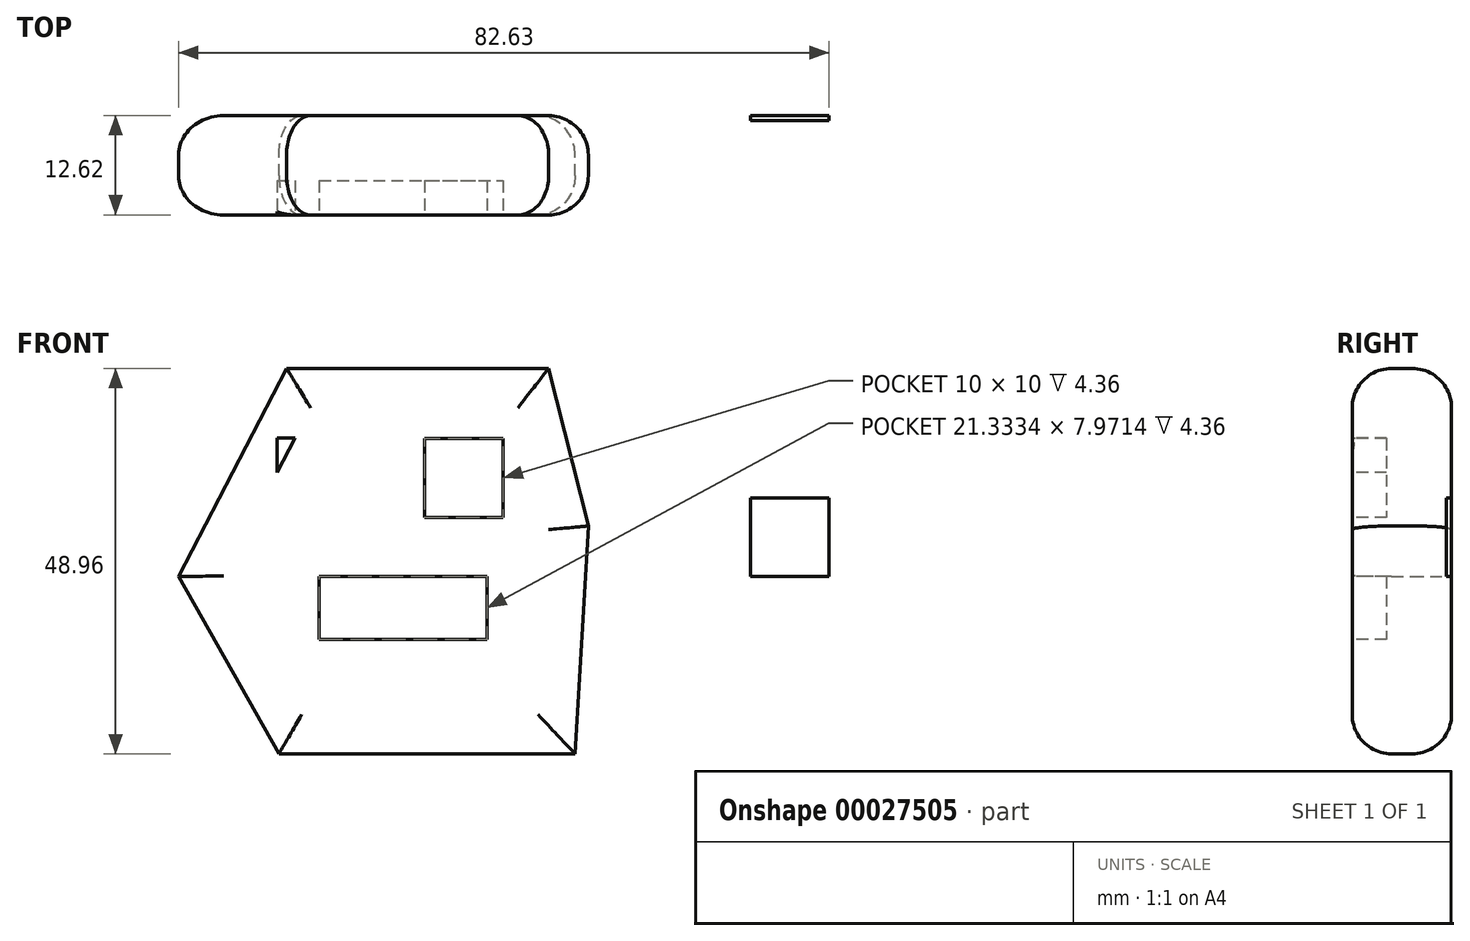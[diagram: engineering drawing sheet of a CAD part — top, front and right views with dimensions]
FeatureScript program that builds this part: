
annotation { "Feature Type Name" : "Feature", "Feature Type Description" : "" }
export const myFeature = defineFeature(function(context is Context, id is Id, definition is map)
    precondition{}
    {
        {
            var Q0;
            Q0=qCreatedBy(makeId("Front.planeOp"),FACE);
            var sketch = newSketch(context, id + "F0", { "sketchPlane" : qUnion([Q0])});
            skLineSegment(sketch, "E0", {"start": v(-17.5, 26.45) * mm, "end": v(15.8, 26.45) * mm});
            skLineSegment(sketch, "E1", {"start": v(15.8, 26.45) * mm, "end": v(20.83, 6.45) * mm});
            skLineSegment(sketch, "E2", {"start": v(20.83, 6.45) * mm, "end": v(19.15, -22.5) * mm});
            skLineSegment(sketch, "E3", {"start": v(19.15, -22.5) * mm, "end": v(-18.48, -22.5) * mm});
            skLineSegment(sketch, "E4", {"start": v(-18.48, -22.5) * mm, "end": v(-31.21, 0) * mm});
            skLineSegment(sketch, "E5", {"start": v(-31.21, 0) * mm, "end": v(-17.5, 26.45) * mm});
            skSolve(sketch);
        }
        {
            var Q0;
            Q0=makeQuery(id+"F0.imprint","IMPRINT",FACE,{"disambiguationData":[TD([[makeQuery(id+"F0.imprint","IMPRINT",EDGE,{"derivedFrom":sQuery(id+"F0.wireOp",EDGE,"E0")}),-1.0]])]});
            extrude(context, id + "F1", {"entities" : qUnion([Q0]), "depth" : 12.62 * mm});
        }
        {
            var Q0;
            Q0=makeQuery(id+"F1.opExtrude","CAP_EDGE",EDGE,{"disambiguationData":[OSD([sQuery(id+"F0.wireOp",EDGE,"E5")])],"isStart":false});
            var Q1;
            Q1=makeQuery(id+"F1.opExtrude","CAP_FACE",FACE,{"disambiguationData":[OSD([sQuery(id+"F0.wireOp",EDGE,"E0"),sQuery(id+"F0.wireOp",EDGE,"E1"),sQuery(id+"F0.wireOp",EDGE,"E2"),sQuery(id+"F0.wireOp",EDGE,"E3"),sQuery(id+"F0.wireOp",EDGE,"E4"),sQuery(id+"F0.wireOp",EDGE,"E5")])],"isStart":false});
            var Q2;
            Q2=makeQuery(id+"F1.opExtrude","CAP_EDGE",EDGE,{"disambiguationData":[OSD([sQuery(id+"F0.wireOp",EDGE,"E1")])],"isStart":true});
            var Q3;
            Q3=makeQuery(id+"F1.opExtrude","CAP_EDGE",EDGE,{"disambiguationData":[OSD([sQuery(id+"F0.wireOp",EDGE,"E0")])],"isStart":true});
            var Q4;
            Q4=makeQuery(id+"F1.opExtrude","CAP_EDGE",EDGE,{"disambiguationData":[OSD([sQuery(id+"F0.wireOp",EDGE,"E4")])],"isStart":true});
            var Q5;
            Q5=makeQuery(id+"F1.opExtrude","CAP_EDGE",EDGE,{"disambiguationData":[OSD([sQuery(id+"F0.wireOp",EDGE,"E5")])],"isStart":true});
            var Q6;
            Q6=makeQuery(id+"F1.opExtrude","CAP_EDGE",EDGE,{"disambiguationData":[OSD([sQuery(id+"F0.wireOp",EDGE,"E2")])],"isStart":true});
            var Q7;
            Q7=makeQuery(id+"F1.opExtrude","CAP_EDGE",EDGE,{"disambiguationData":[OSD([sQuery(id+"F0.wireOp",EDGE,"E3")])],"isStart":true});
            fillet(context, id + "F2", {"entities" : qUnion([Q0, Q1, Q2, Q3, Q4, Q5, Q6, Q7]), "radius" : 5 * mm, "tangentPropagation" : true, "allowEdgeOverflow" : false});
        }
        {
            var Q0;
            Q0=makeQuery(id+"F1.opExtrude","CAP_FACE",FACE,{"disambiguationData":[OSD([sQuery(id+"F0.wireOp",EDGE,"E0"),sQuery(id+"F0.wireOp",EDGE,"E1"),sQuery(id+"F0.wireOp",EDGE,"E2"),sQuery(id+"F0.wireOp",EDGE,"E3"),sQuery(id+"F0.wireOp",EDGE,"E4"),sQuery(id+"F0.wireOp",EDGE,"E5")])],"isStart":false});
            var sketch = newSketch(context, id + "F3", { "sketchPlane" : qUnion([Q0])});
            skLineSegment(sketch, "E6.bottom", {"start": v(-18.7, 17.64) * mm, "end": v(-3.1, 17.64) * mm});
            skLineSegment(sketch, "E6.top", {"start": v(-18.7, 9.53) * mm, "end": v(-3.1, 9.53) * mm});
            skLineSegment(sketch, "E6.left", {"start": v(-18.7, 17.64) * mm, "end": v(-18.7, 9.53) * mm});
            skLineSegment(sketch, "E6.right", {"start": v(-3.1, 17.64) * mm, "end": v(-3.1, 9.53) * mm});
            skLineSegment(sketch, "E7.bottom", {"start": v(-13.37, 0) * mm, "end": v(7.96, 0) * mm});
            skLineSegment(sketch, "E7.top", {"start": v(-13.37, -7.97) * mm, "end": v(7.96, -7.97) * mm});
            skLineSegment(sketch, "E7.left", {"start": v(-13.37, 0) * mm, "end": v(-13.37, -7.97) * mm});
            skLineSegment(sketch, "E7.right", {"start": v(7.96, 0) * mm, "end": v(7.96, -7.97) * mm});
            skLineSegment(sketch, "E8.bottom", {"start": v(0, 17.53) * mm, "end": v(10, 17.53) * mm});
            skLineSegment(sketch, "E8.top", {"start": v(0, 7.53) * mm, "end": v(10, 7.53) * mm});
            skLineSegment(sketch, "E8.left", {"start": v(0, 17.53) * mm, "end": v(0, 7.53) * mm});
            skLineSegment(sketch, "E8.right", {"start": v(10, 17.53) * mm, "end": v(10, 7.53) * mm});
            skSolve(sketch);
        }
        {
            var Q0;
            Q0=makeQuery(id+"F3.imprint","IMPRINT",FACE,{"disambiguationData":[TD([[makeQuery(id+"F3.imprint","IMPRINT",EDGE,{"derivedFrom":sQuery(id+"F3.wireOp",EDGE,"E7.bottom")}),-1.0]])]});
            var Q1;
            Q1=makeQuery(id+"F3.imprint","IMPRINT",FACE,{"disambiguationData":[TD([[makeQuery(id+"F3.imprint","IMPRINT",EDGE,{"derivedFrom":sQuery(id+"F3.wireOp",EDGE,"E8.bottom")}),-1.0]])]});
            var Q2;
            Q2=makeQuery(id+"F3.imprint","IMPRINT",FACE,{"disambiguationData":[TD([[makeQuery(id+"F3.imprint","IMPRINT",EDGE,{"derivedFrom":sQuery(id+"F3.wireOp",EDGE,"E6.bottom")}),-1.0]])]});
            extrude(context, id + "F4", {"entities" : qUnion([Q0, Q1, Q2]), "operationType" : NewBodyOperationType.REMOVE, "oppositeDirection" : true, "depth" : 4.36 * mm});
        }
        {
            var Q0;
            Q0=qCreatedBy(makeId("Front.planeOp"),FACE);
            var sketch = newSketch(context, id + "F5", { "sketchPlane" : qUnion([Q0])});
            skLineSegment(sketch, "E9.bottom", {"start": v(41.42, 10) * mm, "end": v(51.42, 10) * mm});
            skLineSegment(sketch, "E9.top", {"start": v(41.42, 0) * mm, "end": v(51.42, 0) * mm});
            skLineSegment(sketch, "E9.left", {"start": v(41.42, 10) * mm, "end": v(41.42, 0) * mm});
            skLineSegment(sketch, "E9.right", {"start": v(51.42, 10) * mm, "end": v(51.42, 0) * mm});
            skSolve(sketch);
        }
        {
            var Q0;
            Q0=makeQuery(id+"F5.imprint","IMPRINT",FACE,{"disambiguationData":[TD([[makeQuery(id+"F5.imprint","IMPRINT",EDGE,{"derivedFrom":sQuery(id+"F5.wireOp",EDGE,"E9.bottom")}),-1.0]])]});
            extrude(context, id + "F6", {"entities" : qUnion([Q0]), "depth" : 0.64 * mm});
        }
    });
